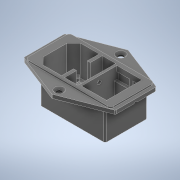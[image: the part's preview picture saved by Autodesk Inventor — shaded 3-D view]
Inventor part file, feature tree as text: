
AUTODESK INVENTOR PART (.ipt)
format: ipt  version: 2021 (Build 250183000, 183)  size: 602,624 bytes
history: native  units: mm
features: extrude x18, sketch x4, mirror x2, revolve x1, boolean_combine x1, projected_geometry x1
ambient origin geometry x8: Origin, YZ Plane, XZ Plane, XY Plane, X Axis, Y Axis, Z Axis, Center Point
bodies: Solid1 (feature_tree), Solid2 (feature_tree)
feature tree (27):
  sketch  "Sketch1"  dims[d0=59.5mm d1=55.3mm]
  extrude  "Extrusion1"  Depth=55.3mm
  extrude  "Extrusion2"  Depth=13.25mm
  revolve  "Revolution1"  [1 undecoded]
  extrude  "Extrusion3"  Depth=1.0mm
  mirror  "Mirror1"
  sketch  "Sketch3"  dims[d4=24.75mm d5=2.0mm]
  extrude  "Extrusion4"  Depth=2.35mm TaperAngle=0.0deg
  extrude  "Extrusion15"  Depth=3.35mm TaperAngle=0.0deg
  extrude  "Extrusion16"  Depth=20.0mm
  extrude  "Extrusion17"  Depth=3.0mm
  extrude  "Extrusion18"  Depth=1.75mm
  extrude  "Extrusion5"  TaperAngle=45.0deg  [1 undecoded]
  extrude  "Extrusion6"  TaperAngle=90.0deg  [1 undecoded]
  extrude  "Extrusion7"  Depth=13.75mm
  extrude  "Extrusion8"  Depth=47.25mm
  extrude  "Extrusion9"  TaperAngle=45.0deg  [1 undecoded]
  extrude  "Extrusion10"  Depth=8.125mm
  extrude  "Extrusion11"  Depth=1.0mm
  extrude  "Extrusion12"  Depth=18.75mm TaperAngle=0.0deg
  extrude  "Extrusion13"  Depth=11.5mm
  mirror  "Mirror2"
  boolean_combine  "Combine1"
  extrude  "Extrusion14"  Depth=16.25mm
  sketch  "Sketch2"  dims[d2=14.25mm d3=13.25mm]
  projected_geometry  "Projected Loop1"
  sketch  "Sketch4"  dims[d6=1.0mm d7=1.0mm d8=2.35mm d9=0.0mm d10=3.35mm d11=0.0mm d12=20.0mm d13=3.0mm d14=1.75mm d16=45.0deg d17=90.0deg d18=13.75mm d19=47.25mm d20=45.0deg d21=8.125mm d22=1.0mm d23=18.75mm d24=0.0mm d25=11.5mm d26=16.25mm d27=7.5mm d28=1.5mm d29=2.0mm d30=8.75mm d31=12.25mm d32=4.5mm d33=45.0deg d34=7.0mm d35=7.75mm d36=19.75mm d37=0.0mm d38=19.25mm d39=0.0mm d40=9.625mm d41=11.5mm d42=0.0mm d43=0.75mm d44=6.0mm d45=6.0mm d46=0.5mm d47=0.25mm d48=0.5mm d49=4.0mm d50=2.0mm d51=2.0mm d52=1.5mm d53=2.0mm d54=6.0mm d55=5.0mm d56=0.0mm d57=18.6mm d58=0.0mm d59=1.75mm d60=0.0mm d61=0.625mm d62=0.625mm d63=1.75mm d64=0.0mm d65=1.75mm d66=0.0mm d67=0.5mm d68=0.0mm d69=4.5mm d70=0.0mm d71=2.5mm d72=2.5mm d73=1.5mm d75=1.75mm d76=0.0mm d77=2.5mm d78=0.5mm d79=1.75mm d80=0.0mm d81=8.0mm d82=8.0mm d83=0.75mm d84=0.75mm d85=5.0mm d86=2.5mm d87=4.0mm d88=6.0mm d89=6.0mm d90=7.0mm d91=1.25mm d92=2.0mm d93=2.0mm d94=2.0mm d95=0.5mm d96=10.0mm d97=0.0mm d98=1.0mm d99=0.0mm d100=0.5mm d101=0.0mm d102=2.0mm d103=0.0mm]
note: 4 required parameter values undecoded (feature->parameter linkage not recoverable at this tier; creation-order binding heuristic only, values carry confidence <= 0.55)